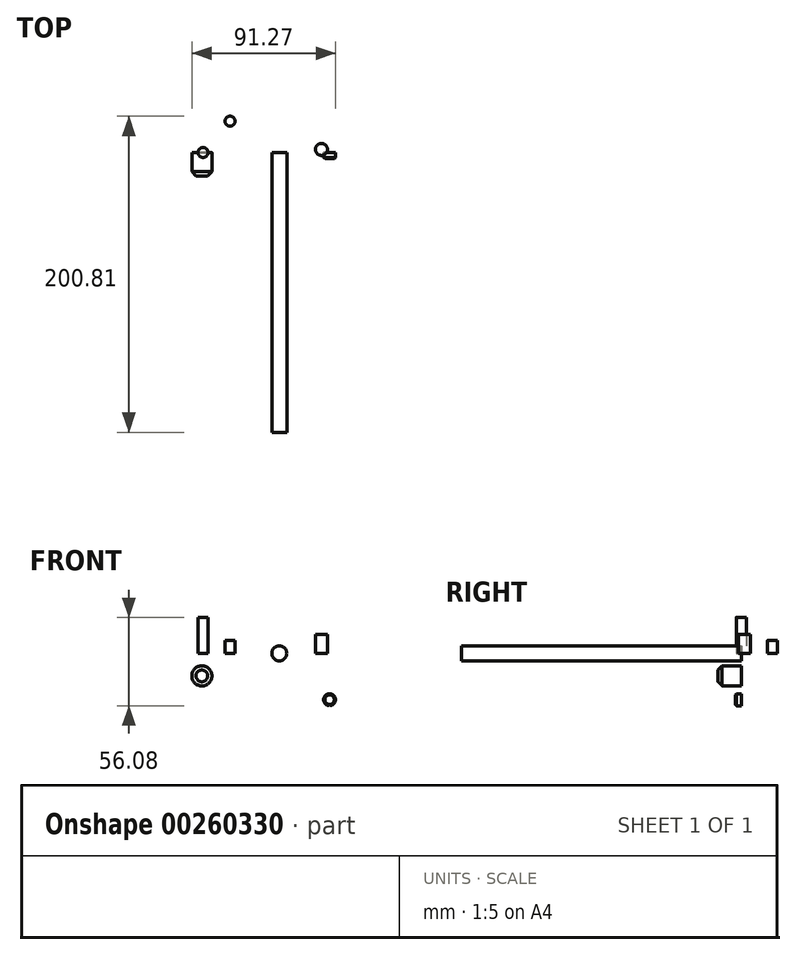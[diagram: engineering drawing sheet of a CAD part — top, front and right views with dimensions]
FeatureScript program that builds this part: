
annotation { "Feature Type Name" : "Feature", "Feature Type Description" : "" }
export const myFeature = defineFeature(function(context is Context, id is Id, definition is map)
    precondition{}
    {
        {
            var Q0;
            Q0=qCreatedBy(makeId("Front.planeOp"),FACE);
            var sketch = newSketch(context, id + "F0", { "sketchPlane" : qUnion([Q0])});
            skCircle(sketch, "E0", {"center": v(0, 0) * mm, "radius": 4.76 * mm});
            skSolve(sketch);
        }
        {
            var Q0;
            Q0 = qSketchRegion(id + "F0", true);
            extrude(context, id + "F1", {"entities" : qUnion([Q0]), "depth" : 177.8 * mm});
        }
        {
            var Q0;
            Q0=qCreatedBy(makeId("Top.planeOp"),FACE);
            var sketch = newSketch(context, id + "F2", { "sketchPlane" : qUnion([Q0])});
            skCircle(sketch, "E1", {"center": v(-48.44, 0) * mm, "radius": 3.18 * mm});
            skSolve(sketch);
        }
        {
            var Q0;
            Q0=sQuery(id+"F2.wireOp",EDGE,"E1");
            extrude(context, id + "F3", {"bodyType" : ToolBodyType.SURFACE, "surfaceEntities" : qUnion([Q0]), "depth" : 22.86 * mm});
        }
        {
            var Q0;
            Q0=qCreatedBy(makeId("Top.planeOp"),FACE);
            var sketch = newSketch(context, id + "F4", { "sketchPlane" : qUnion([Q0])});
            skCircle(sketch, "E2", {"center": v(-31.28, 19.84) * mm, "radius": 3.18 * mm});
            skSolve(sketch);
        }
        {
            var Q0;
            Q0 = qSketchRegion(id + "F4", true);
            extrude(context, id + "F5", {"entities" : qUnion([Q0]), "depth" : 8.25 * mm});
        }
        {
            var Q0;
            Q0 = qSketchRegion(id + "F2", true);
            extrude(context, id + "F6", {"entities" : qUnion([Q0]), "depth" : 22.86 * mm});
        }
        {
            var Q0;
            Q0=makeQuery(id+"F3.opExtrude","SWEPT_BODY",BODY,{"disambiguationData":[OSD([sQuery(id+"F2.wireOp",EDGE,"E1")])]});
            deleteBodies(context, id + "F7", {"entities" : qUnion([Q0])});
        }
        {
            var Q0;
            Q0=qCreatedBy(makeId("Top.planeOp"),FACE);
            var sketch = newSketch(context, id + "F8", { "sketchPlane" : qUnion([Q0])});
            skCircle(sketch, "E3", {"center": v(26.78, 1.89) * mm, "radius": 3.78 * mm});
            skSolve(sketch);
        }
        {
            var Q0;
            Q0 = qSketchRegion(id + "F8", true);
            extrude(context, id + "F9", {"entities" : qUnion([Q0]), "depth" : 12.13 * mm});
        }
        {
            var Q0;
            Q0=qCreatedBy(makeId("Front.planeOp"),FACE);
            var sketch = newSketch(context, id + "F10", { "sketchPlane" : qUnion([Q0])});
            skCircle(sketch, "E4", {"center": v(-49.2, -14.32) * mm, "radius": 6.38 * mm});
            skSolve(sketch);
        }
        {
            var Q0;
            Q0 = qSketchRegion(id + "F10", true);
            extrude(context, id + "F11", {"entities" : qUnion([Q0]), "depth" : 14.9 * mm});
        }
        {
            var Q0;
            Q0=makeQuery(id+"F11.opExtrude","CAP_EDGE",EDGE,{"disambiguationData":[OSD([sQuery(id+"F10.wireOp",EDGE,"E4")])],"isStart":false});
            chamfer(context, id + "F12", {"entities" : qUnion([Q0]), "width" : 2.67 * mm, "tangentPropagation" : true});
        }
        {
            var Q0;
            Q0=qCreatedBy(makeId("Front.planeOp"),FACE);
            var sketch = newSketch(context, id + "F13", { "sketchPlane" : qUnion([Q0])});
            skCircle(sketch, "E5", {"center": v(31.91, -29.44) * mm, "radius": 3.78 * mm});
            skSolve(sketch);
        }
        {
            var Q0;
            Q0 = qSketchRegion(id + "F13", true);
            extrude(context, id + "F14", {"entities" : qUnion([Q0]), "depth" : 3.92 * mm});
        }
        {
            var Q0;
            Q0=makeQuery(id+"F14.opExtrude","CAP_EDGE",EDGE,{"disambiguationData":[OSD([sQuery(id+"F13.wireOp",EDGE,"E5")])],"isStart":false});
            chamfer(context, id + "F15", {"entities" : qUnion([Q0]), "width" : 0.76 * mm, "tangentPropagation" : true});
        }
    });
